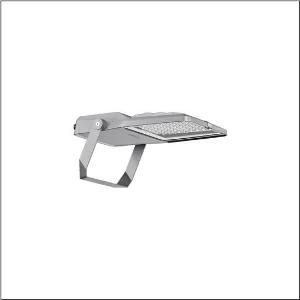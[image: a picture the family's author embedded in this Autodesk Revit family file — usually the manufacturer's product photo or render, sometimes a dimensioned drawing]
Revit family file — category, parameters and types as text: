
# Revit family: floodlight_fl_21_mini___pl43_5xa7774c2a1a_b50a
name_source: partatom
category: Lighting Fixtures
units: mm (PartAtom-declared; Revit-internal decimal feet)

## family parameters
Cut with Voids When Loaded = No
Host = Face
Light Source = No
Part Type = Normal
Room Calculation Point = No
Round Connector Dimension = Use Diameter
Shared = No

## types (1)
- --- (1 x LED, 12480 lm, 88.8 W, 3000K)
    Apparent Load = 89 VA
    CIE Flux Codes = 27 78 99 100 100
    Color Rendering = 70
    Color Temperature = 3000K
    Default Elevation = 1800 mm
    Description = Floodlight FL 21 mini, floodlight, primary light control with lens, of PMMA, primary optical cover: protective disc, of toughened safety glass, transparent, light distribution: PL43, light emission: direct distribution, installation type: surface-mounted, LED, High Power LED, rated luminous flux: 12.480lm, luminous efficacy: 141lm/W, light colour: 730, colour temperature: 3000K, control gear: ECG DALI, control: overheat protection, power reduction, constant luminous flux control, flexible luminous flux parameterisation, with terminal, 6-pole, mains connection: 220..240V, AC/DC, 0/50..60Hz, start of lifetime: 89W, end of service life: 94W, reduction: 42W, luminaire housing, of diecast aluminium, powder-coated, Siteco® metallic grey (DB 702S), corrosivity category C5 mid according to DIN EN ISO 12944, sealing non-destructively replaceable, mounting bracket, of steel, galvanised, powder-coated, Siteco® metallic grey (DB 702S), protection rating (complete): IP66, insulation class (complete): insulation class II (safety insulation), certification: CE, ENEC, VDE, impact resistance: IK08, permissible operating ambient temperature: -40..+40°C, permissible operating ambient temperature for outdoor applications: -40..+50°C, standard: DIN EN 12944, LABS conformity tested according to VDMA 24364:2018-05, packaging unit: 1 piece

Light Distribution: PL43
    Height = 70 mm
    Lamp = 1 x LED
    Lamp Light Flux = 12480 lm
    Lamp Power = 88.8 W
    Lamp count = 1
    Length = 485 mm
    Luminous efficacy = 141 lm/W
    Manufacturer = Siteco
    ModVariant = No
    Model = 5XA7774C2A1A
    Number of Poles = 1
    OnlyDefault = Yes
    Power Factor = 1
    Product Name = Floodlight FL 21 mini | PL43
    Product group = floodlight | pylon annexe
    ProductGroupID = 6200
    Protection Class = Protection class II
    Protection Degree = IP 66
    RLX_Detail_Level = 1
    RLX_Emergency_Light_Flux = 0 lm
    RLX_Emergency_Type = 0
    RLX_Emergency_Type_DB = No
    RlxData = <blob elided: 95949 chars, md5=0f25a618>
    Socket = socket
    Standby Power = 0 W
    System Light Flux = 12480 lm
    System Power = 89 W
    Type Comments = factory setting: luminous flux: 100 % | dim-lin: 254 | 456 mA
    Type Image = l_1006845.jpg
    URL = http://relux.com
    VarID = @adj_094533
    Voltage = 0 V
    Weight = 0.00 kg
    Width = 337 mm

## geometry (parser evidence)
native form markers: Blend x4, Sweep x11
no freeform markers — native parametric forms only
